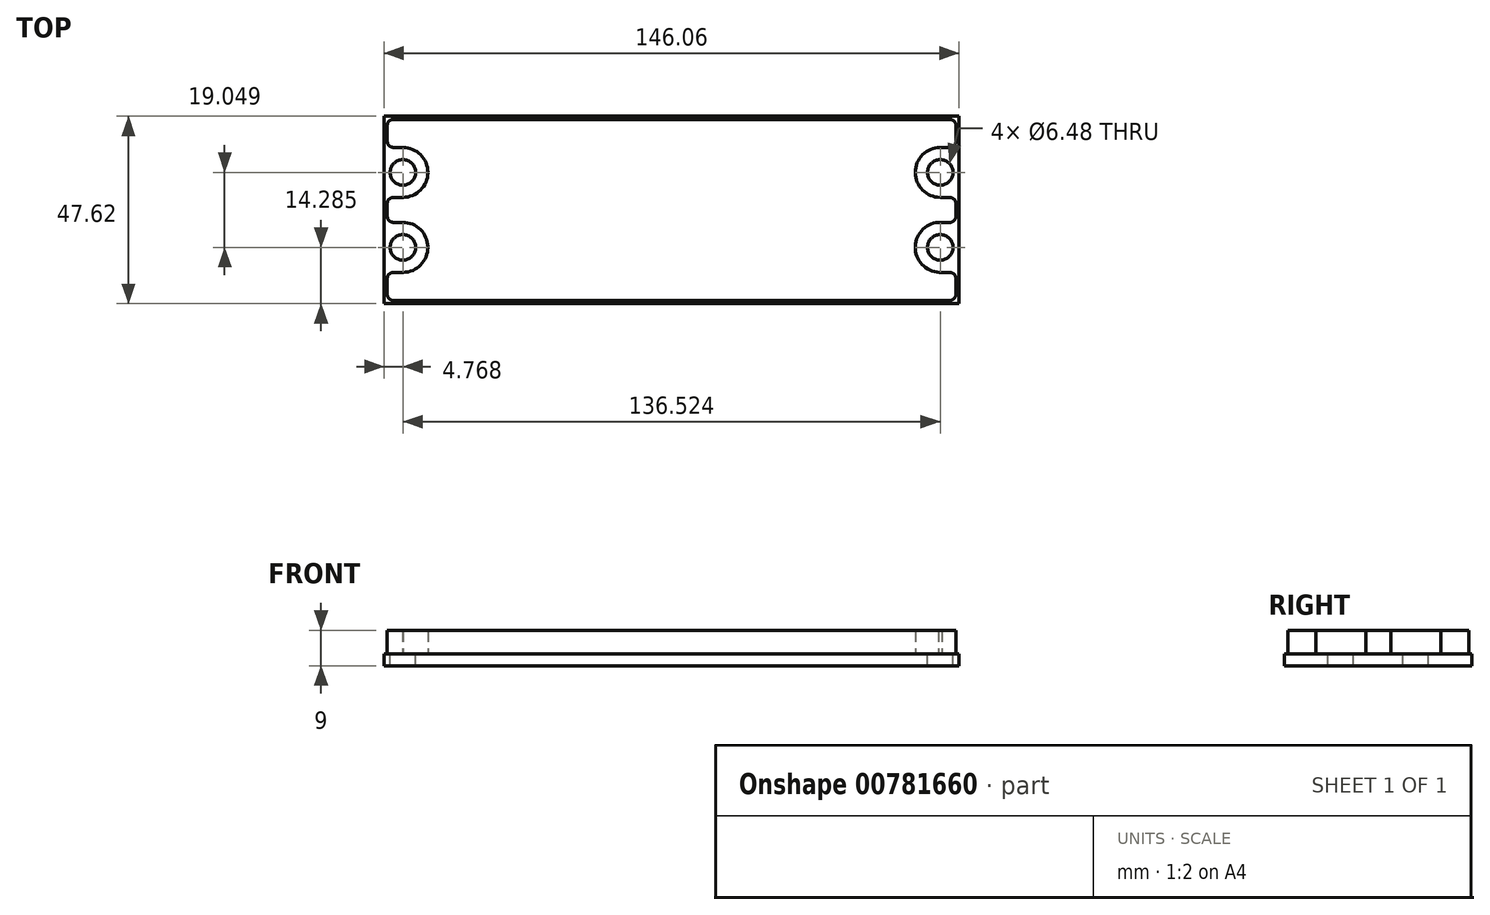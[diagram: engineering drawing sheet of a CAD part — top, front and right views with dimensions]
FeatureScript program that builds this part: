
annotation { "Feature Type Name" : "Feature", "Feature Type Description" : "" }
export const myFeature = defineFeature(function(context is Context, id is Id, definition is map)
    precondition{}
    {
        {
            var Q0;
            Q0=qCreatedBy(makeId("Top.planeOp"),FACE);
            var sketch = newSketch(context, id + "F0", { "sketchPlane" : qUnion([Q0])});
            skLineSegment(sketch, "E0", {"start": v(72.22, -23.01) * mm, "end": v(72.22, -15.86) * mm});
            skLineSegment(sketch, "E1", {"start": v(72.22, -3.19) * mm, "end": v(72.22, 3.17) * mm});
            skLineSegment(sketch, "E2", {"start": v(-68.2, -15.87) * mm, "end": v(-72.23, -15.87) * mm});
            skLineSegment(sketch, "E3", {"start": v(-68.26, 15.87) * mm, "end": v(-72.23, 15.87) * mm});
            skLineSegment(sketch, "E4", {"start": v(68.26, 15.87) * mm, "end": v(72.22, 15.87) * mm});
            skLineSegment(sketch, "E5", {"start": v(-68.26, 3.17) * mm, "end": v(-72.23, 3.17) * mm});
            skLineSegment(sketch, "E6", {"start": v(68.26, 3.17) * mm, "end": v(72.22, 3.17) * mm});
            skLineSegment(sketch, "E7", {"start": v(67.83, -3.19) * mm, "end": v(72.22, -3.19) * mm});
            skArc(sketch, "E8", {"start": v(67.83, -3.19) * mm, "mid": v(61.93, -9.96) * mm, "end": v(68.7, -15.86) * mm});
            skLineSegment(sketch, "E9", {"start": v(68.7, -15.86) * mm, "end": v(72.22, -15.86) * mm});
            skLineSegment(sketch, "E10", {"start": v(-68.33, -3.17) * mm, "end": v(-72.23, -3.17) * mm});
            skArc(sketch, "E11", {"start": v(68.26, 15.87) * mm, "mid": v(61.91, 9.52) * mm, "end": v(68.26, 3.17) * mm});
            skLineSegment(sketch, "E12", {"start": v(72.22, 15.87) * mm, "end": v(72.22, 23.01) * mm});
            skLineSegment(sketch, "E13", {"start": v(-72.23, -3.17) * mm, "end": v(-72.23, 3.17) * mm});
            skLineSegment(sketch, "E14", {"start": v(-72.23, 15.87) * mm, "end": v(-72.23, 23.01) * mm});
            skLineSegment(sketch, "E15", {"start": v(72.22, -23.01) * mm, "end": v(-72.23, -23.01) * mm});
            skArc(sketch, "E16", {"start": v(-68.26, 3.17) * mm, "mid": v(-61.91, 9.52) * mm, "end": v(-68.26, 15.87) * mm});
            skLineSegment(sketch, "E17", {"start": v(-72.23, 23.01) * mm, "end": v(72.23, 23.01) * mm});
            skArc(sketch, "E18", {"start": v(-68.2, -15.87) * mm, "mid": v(-61.91, -9.46) * mm, "end": v(-68.33, -3.17) * mm});
            skLineSegment(sketch, "E19", {"start": v(-72.23, -23.01) * mm, "end": v(-72.23, -15.87) * mm});
            skCircle(sketch, "E20", {"center": v(68.26, -9.52) * mm, "radius": 3.24 * mm});
            skCircle(sketch, "E21", {"center": v(-68.26, 9.52) * mm, "radius": 3.24 * mm});
            skLineSegment(sketch, "E22", {"start": v(-73.03, -23.81) * mm, "end": v(-73.03, 23.81) * mm});
            skCircle(sketch, "E23", {"center": v(-68.26, -9.52) * mm, "radius": 3.24 * mm});
            skLineSegment(sketch, "E24", {"start": v(73.03, -23.81) * mm, "end": v(73.03, 23.81) * mm});
            skLineSegment(sketch, "E25", {"start": v(-73.03, 23.81) * mm, "end": v(73.03, 23.81) * mm});
            skLineSegment(sketch, "E26", {"start": v(73.03, -23.81) * mm, "end": v(-73.03, -23.81) * mm});
            skCircle(sketch, "E27", {"center": v(68.26, 9.52) * mm, "radius": 3.24 * mm});
            skSolve(sketch);
        }
        {
            var Q0;
            Q0=makeQuery(id+"F0.imprint","IMPRINT",FACE,{"disambiguationData":[TD([[makeQuery(id+"F0.imprint","IMPRINT",EDGE,{"derivedFrom":sQuery(id+"F0.wireOp",EDGE,"E0")}),-1.0]])]});
            var Q1;
            Q1=makeQuery(id+"F0.imprint","IMPRINT",FACE,{"disambiguationData":[TD([[makeQuery(id+"F0.imprint","IMPRINT",EDGE,{"derivedFrom":sQuery(id+"F0.wireOp",EDGE,"E0")}),1.0]])]});
            extrude(context, id + "F1", {"entities" : qUnion([Q0, Q1]), "oppositeDirection" : true, "depth" : 3 * mm, "offsetDistance" : 25 * mm});
        }
        {
            var Q0;
            Q0=makeQuery(id+"F0.imprint","IMPRINT",FACE,{"disambiguationData":[TD([[makeQuery(id+"F0.imprint","IMPRINT",EDGE,{"derivedFrom":sQuery(id+"F0.wireOp",EDGE,"E0")}),1.0]])]});
            extrude(context, id + "F2", {"entities" : qUnion([Q0]), "depth" : 6 * mm, "offsetDistance" : 25 * mm});
        }
        {
            var Q0;
            Q0=makeQuery(id+"F2.opExtrude","SWEPT_EDGE",EDGE,{"disambiguationData":[OSD([sQuery(id+"F0.wireOp",EDGE,"E17"),sQuery(id+"F0.wireOp",EDGE,"E14")])]});
            var Q1;
            Q1=makeQuery(id+"F2.opExtrude","SWEPT_EDGE",EDGE,{"disambiguationData":[OSD([sQuery(id+"F0.wireOp",EDGE,"E3"),sQuery(id+"F0.wireOp",EDGE,"E14")])]});
            var Q2;
            Q2=makeQuery(id+"F2.opExtrude","SWEPT_EDGE",EDGE,{"disambiguationData":[OSD([sQuery(id+"F0.wireOp",EDGE,"E5"),sQuery(id+"F0.wireOp",EDGE,"E13")])]});
            var Q3;
            Q3=makeQuery(id+"F2.opExtrude","SWEPT_EDGE",EDGE,{"disambiguationData":[OSD([sQuery(id+"F0.wireOp",EDGE,"E13"),sQuery(id+"F0.wireOp",EDGE,"E10")])]});
            var Q4;
            Q4=makeQuery(id+"F2.opExtrude","SWEPT_EDGE",EDGE,{"disambiguationData":[OSD([sQuery(id+"F0.wireOp",EDGE,"E19"),sQuery(id+"F0.wireOp",EDGE,"E2")])]});
            var Q5;
            Q5=makeQuery(id+"F2.opExtrude","SWEPT_EDGE",EDGE,{"disambiguationData":[OSD([sQuery(id+"F0.wireOp",EDGE,"E19"),sQuery(id+"F0.wireOp",EDGE,"E15")])]});
            var Q6;
            Q6=makeQuery(id+"F2.opExtrude","SWEPT_EDGE",EDGE,{"disambiguationData":[OSD([sQuery(id+"F0.wireOp",EDGE,"E0"),sQuery(id+"F0.wireOp",EDGE,"E15")])]});
            var Q7;
            Q7=makeQuery(id+"F2.opExtrude","SWEPT_EDGE",EDGE,{"disambiguationData":[OSD([sQuery(id+"F0.wireOp",EDGE,"E0"),sQuery(id+"F0.wireOp",EDGE,"E9")])]});
            var Q8;
            Q8=makeQuery(id+"F2.opExtrude","SWEPT_EDGE",EDGE,{"disambiguationData":[OSD([sQuery(id+"F0.wireOp",EDGE,"E7"),sQuery(id+"F0.wireOp",EDGE,"E1")])]});
            var Q9;
            Q9=makeQuery(id+"F2.opExtrude","SWEPT_EDGE",EDGE,{"disambiguationData":[OSD([sQuery(id+"F0.wireOp",EDGE,"E1"),sQuery(id+"F0.wireOp",EDGE,"E6")])]});
            var Q10;
            Q10=makeQuery(id+"F2.opExtrude","SWEPT_EDGE",EDGE,{"disambiguationData":[OSD([sQuery(id+"F0.wireOp",EDGE,"E17"),sQuery(id+"F0.wireOp",EDGE,"E12")])]});
            var Q11;
            Q11=makeQuery(id+"F2.opExtrude","SWEPT_EDGE",EDGE,{"disambiguationData":[OSD([sQuery(id+"F0.wireOp",EDGE,"E4"),sQuery(id+"F0.wireOp",EDGE,"E12")])]});
            fillet(context, id + "F3", {"entities" : qUnion([Q0, Q1, Q2, Q3, Q4, Q5, Q6, Q7, Q8, Q9, Q10, Q11]), "radius" : 1.59 * mm, "tangentPropagation" : true, "allowEdgeOverflow" : false});
        }
    });
